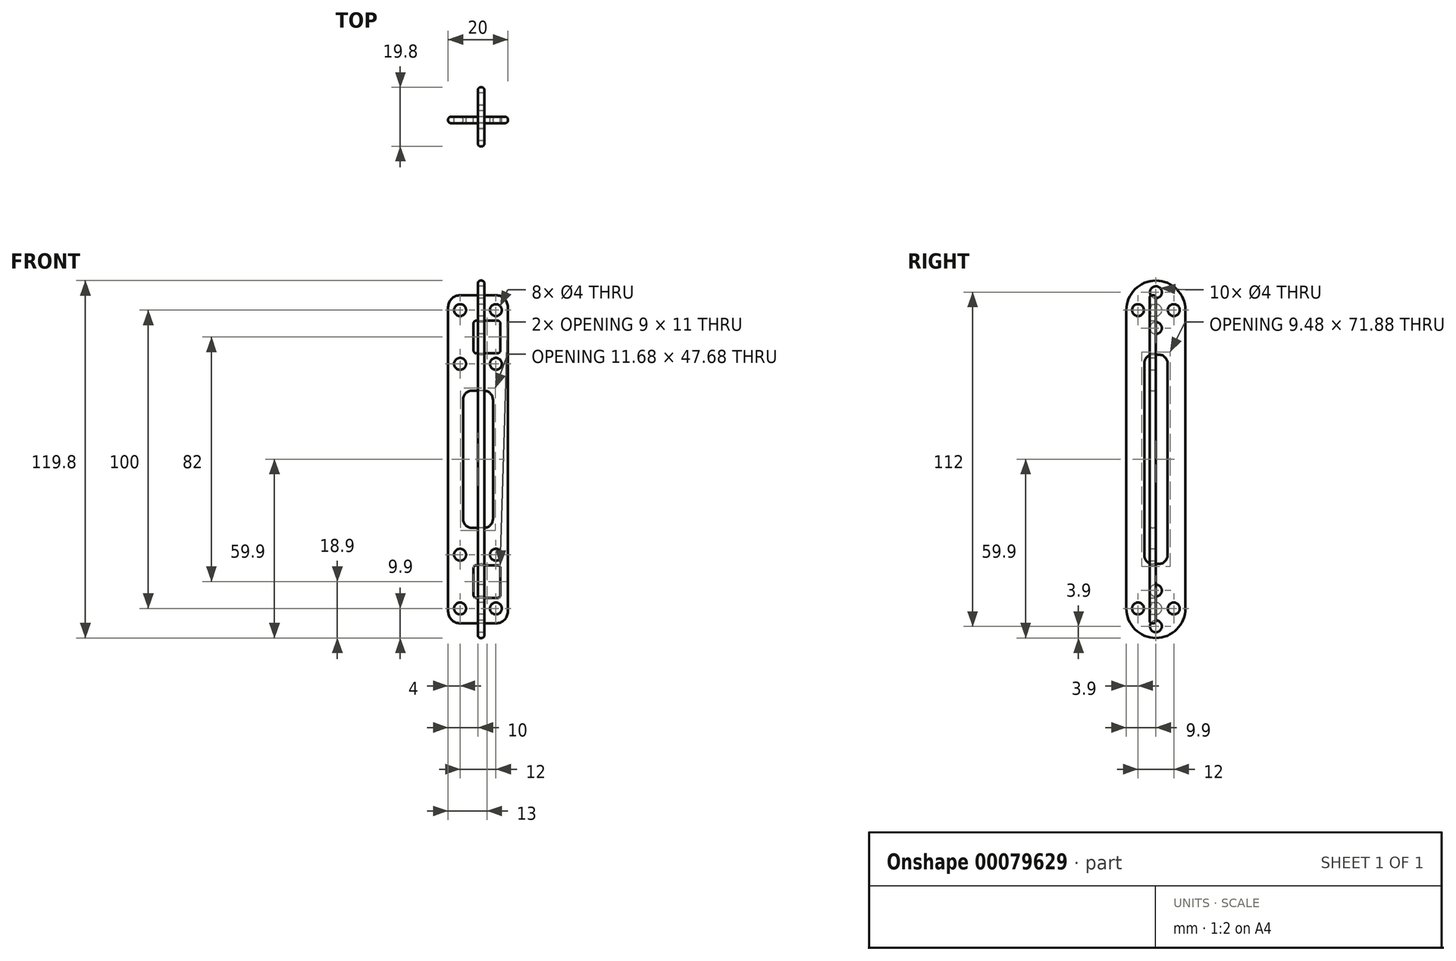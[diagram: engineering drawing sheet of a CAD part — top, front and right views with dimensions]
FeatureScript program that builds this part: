
annotation { "Feature Type Name" : "Feature", "Feature Type Description" : "" }
export const myFeature = defineFeature(function(context is Context, id is Id, definition is map)
    precondition{}
    {
        {
            assignVariable(context, id + "F0", {"name" : "tolerance", "anyValue" : 0.1});
        }
        {
            assignVariable(context, id + "F1", {"name" : "thickness", "anyValue" : 2.2 - getVariable(context, 'tolerance')});
        }
        {
            var Q0;
            Q0=qCreatedBy(makeId("Right.planeOp"),FACE);
            var sketch = newSketch(context, id + "F2", { "sketchPlane" : qUnion([Q0])});
            skLineSegment(sketch, "E0.rect.bottom", {"start": v(12, -9) * mm, "end": v(-12, -9) * mm});
            skLineSegment(sketch, "E0.rect.top", {"start": v(12, 27) * mm, "end": v(-12, 27) * mm});
            skLineSegment(sketch, "E0.rect.left", {"start": v(12, -9) * mm, "end": v(12, 27) * mm});
            skLineSegment(sketch, "E0.rect.right", {"start": v(-12, -9) * mm, "end": v(-12, 27) * mm});
            skPoint(sketch, "E0.rect.middle", {"position": v(0, 9) * mm});
            skCircle(sketch, "E1", {"center": v(0, 0) * mm, "radius": 8.9 * mm});
            skLineSegment(sketch, "E2", {"start": v(0, 27) * mm, "end": v(0, -9) * mm, "construction": true});
            skCircle(sketch, "E3", {"center": v(0, 0) * mm, "radius": 6 * mm, "construction": true});
            skCircle(sketch, "E4", {"center": v(0, -6) * mm, "radius": 2 * mm});
            skCircle(sketch, "E5.1.0", {"center": v(6, 0) * mm, "radius": 2 * mm});
            skCircle(sketch, "E5.2.0", {"center": v(0, 6) * mm, "radius": 2 * mm});
            skCircle(sketch, "E5.3.0", {"center": v(-6, 0) * mm, "radius": 2 * mm});
            skCircle(sketch, "E6", {"center": v(-4.24, 4.24) * mm, "radius": 0.8 * mm});
            skCircle(sketch, "E7.1.0", {"center": v(-4.24, -4.24) * mm, "radius": 0.8 * mm});
            skCircle(sketch, "E7.2.0", {"center": v(4.24, -4.24) * mm, "radius": 0.8 * mm});
            skCircle(sketch, "E7.3.0", {"center": v(4.24, 4.24) * mm, "radius": 0.8 * mm});
            skLineSegment(sketch, "E8", {"start": v(-6, 24) * mm, "end": v(6, 24) * mm, "construction": true});
            skCircle(sketch, "E9", {"center": v(-6, 24) * mm, "radius": 2 * mm});
            skCircle(sketch, "E10", {"center": v(0, 24) * mm, "radius": 2 * mm});
            skCircle(sketch, "E11", {"center": v(6, 24) * mm, "radius": 2 * mm});
            skPoint(sketch, "E12.center", {"position": v(0, 100) * mm});
            skLineSegment(sketch, "E13.rect.right", {"start": v(12, 109) * mm, "end": v(12, 73) * mm});
            skCircle(sketch, "E14", {"center": v(-6, 76) * mm, "radius": 2 * mm});
            skLineSegment(sketch, "E15", {"start": v(0, 73) * mm, "end": v(0, 109) * mm, "construction": true});
            skCircle(sketch, "E16", {"center": v(0, 100) * mm, "radius": 8.9 * mm});
            skLineSegment(sketch, "E13.rect.left", {"start": v(-12, 109) * mm, "end": v(-12, 73) * mm});
            skLineSegment(sketch, "E13.rect.bottom", {"start": v(-12, 109) * mm, "end": v(12, 109) * mm});
            skLineSegment(sketch, "E13.rect.top", {"start": v(-12, 73) * mm, "end": v(12, 73) * mm});
            skLineSegment(sketch, "E17", {"start": v(6, 76) * mm, "end": v(-6, 76) * mm, "construction": true});
            skCircle(sketch, "E18", {"center": v(0, 76) * mm, "radius": 2 * mm});
            skPoint(sketch, "E13.rect.middle", {"position": v(0, 91) * mm});
            skCircle(sketch, "E12.2.0", {"center": v(0, 94) * mm, "radius": 2 * mm});
            skCircle(sketch, "E12.1.0", {"center": v(-6, 100) * mm, "radius": 2 * mm});
            skCircle(sketch, "E19", {"center": v(0, 100) * mm, "radius": 6 * mm, "construction": true});
            skCircle(sketch, "E20", {"center": v(0, 106) * mm, "radius": 2 * mm});
            skCircle(sketch, "E21", {"center": v(-4.24, 104.24) * mm, "radius": 0.8 * mm});
            skCircle(sketch, "E12.3.0", {"center": v(6, 100) * mm, "radius": 2 * mm});
            skCircle(sketch, "E22.3.0", {"center": v(4.24, 104.24) * mm, "radius": 0.8 * mm});
            skCircle(sketch, "E22.2.0", {"center": v(4.24, 95.76) * mm, "radius": 0.8 * mm});
            skCircle(sketch, "E22.1.0", {"center": v(-4.24, 95.76) * mm, "radius": 0.8 * mm});
            skCircle(sketch, "E23", {"center": v(6, 76) * mm, "radius": 2 * mm});
            skSolve(sketch);
        }
        {
            var Q0;
            Q0=qCreatedBy(makeId("Front.planeOp"),FACE);
            var sketch = newSketch(context, id + "F3", { "sketchPlane" : qUnion([Q0])});
            skLineSegment(sketch, "E24", {"start": v(0, 22.5) * mm, "end": v(9, 22.5) * mm});
            skLineSegment(sketch, "E25", {"start": v(9, 22.5) * mm, "end": v(9, 27) * mm});
            skLineSegment(sketch, "E26", {"start": v(9, 27) * mm, "end": v(12, 27) * mm});
            skLineSegment(sketch, "E27", {"start": v(12, 27) * mm, "end": v(12, -9) * mm});
            skLineSegment(sketch, "E28", {"start": v(12, -9) * mm, "end": v(0, -9) * mm});
            skLineSegment(sketch, "E29", {"start": v(12, 8.9) * mm, "end": v(15, 8.9) * mm});
            skLineSegment(sketch, "E30", {"start": v(15, 8.9) * mm, "end": v(15, -8.9) * mm});
            skLineSegment(sketch, "E31", {"start": v(15, -8.9) * mm, "end": v(12, -8.9) * mm});
            skLineSegment(sketch, "E32", {"start": v(0, 1.45) * mm, "end": v(0, -56.88) * mm, "construction": true});
            skLineSegment(sketch, "E33", {"start": v(0, 0) * mm, "end": v(15, 0) * mm, "construction": true});
            skLineSegment(sketch, "E34.MirrorCS", {"start": v(-15, 8.9) * mm, "end": v(-15, -8.9) * mm});
            skLineSegment(sketch, "E35.MirrorCS", {"start": v(0, 22.5) * mm, "end": v(-9, 22.5) * mm});
            skLineSegment(sketch, "E36.MirrorCS", {"start": v(0, 0) * mm, "end": v(-15, 0) * mm, "construction": true});
            skLineSegment(sketch, "E37.MirrorCS", {"start": v(-9, 22.5) * mm, "end": v(-9, 27) * mm});
            skLineSegment(sketch, "E38.MirrorCS", {"start": v(-12, 8.9) * mm, "end": v(-15, 8.9) * mm});
            skLineSegment(sketch, "E39.MirrorCS", {"start": v(-12, -9) * mm, "end": v(0, -9) * mm});
            skLineSegment(sketch, "E40.MirrorCS", {"start": v(-12, 27) * mm, "end": v(-12, -9) * mm});
            skLineSegment(sketch, "E41.MirrorCS", {"start": v(-15, -8.9) * mm, "end": v(-12, -8.9) * mm});
            skLineSegment(sketch, "E42.MirrorCS", {"start": v(-9, 27) * mm, "end": v(-12, 27) * mm});
            skLineSegment(sketch, "E43.MirrorCS", {"start": v(0, 100) * mm, "end": v(-15, 100) * mm, "construction": true});
            skLineSegment(sketch, "E44.MirrorCS", {"start": v(0, 77.5) * mm, "end": v(-9, 77.5) * mm});
            skLineSegment(sketch, "E45", {"start": v(15, 108.9) * mm, "end": v(15, 91.1) * mm});
            skLineSegment(sketch, "E46.MirrorCS", {"start": v(-15, 108.9) * mm, "end": v(-15, 91.1) * mm});
            skLineSegment(sketch, "E47", {"start": v(0, 57.8) * mm, "end": v(0, 0) * mm, "construction": true});
            skLineSegment(sketch, "E48", {"start": v(12, 109) * mm, "end": v(0, 109) * mm});
            skLineSegment(sketch, "E49", {"start": v(12, 109) * mm, "end": v(12, 73) * mm});
            skLineSegment(sketch, "E50", {"start": v(0, 77.5) * mm, "end": v(9, 77.5) * mm});
            skLineSegment(sketch, "E51.MirrorCS", {"start": v(-12, 109) * mm, "end": v(0, 109) * mm});
            skLineSegment(sketch, "E52.MirrorCS", {"start": v(-12, 109) * mm, "end": v(-12, 73) * mm});
            skLineSegment(sketch, "E53", {"start": v(0, 100) * mm, "end": v(15, 100) * mm, "construction": true});
            skLineSegment(sketch, "E54", {"start": v(12, 108.9) * mm, "end": v(15, 108.9) * mm});
            skLineSegment(sketch, "E55", {"start": v(9, 73) * mm, "end": v(12, 73) * mm});
            skLineSegment(sketch, "E56", {"start": v(9, 73) * mm, "end": v(9, 77.5) * mm});
            skLineSegment(sketch, "E57.MirrorCS", {"start": v(-9, 73) * mm, "end": v(-12, 73) * mm});
            skLineSegment(sketch, "E58.MirrorCS", {"start": v(-12, 108.9) * mm, "end": v(-15, 108.9) * mm});
            skLineSegment(sketch, "E59.MirrorCS", {"start": v(-9, 73) * mm, "end": v(-9, 77.5) * mm});
            skLineSegment(sketch, "E60.MirrorCS", {"start": v(-15, 91.1) * mm, "end": v(-12, 91.1) * mm});
            skLineSegment(sketch, "E61", {"start": v(15, 91.1) * mm, "end": v(12, 91.1) * mm});
            skLineSegment(sketch, "E62.bottom", {"start": v(-6, 18) * mm, "end": v(6, 18) * mm, "construction": true});
            skLineSegment(sketch, "E62.top", {"start": v(-6, 0) * mm, "end": v(6, 0) * mm, "construction": true});
            skLineSegment(sketch, "E62.left", {"start": v(-6, 18) * mm, "end": v(-6, 0) * mm, "construction": true});
            skLineSegment(sketch, "E62.right", {"start": v(6, 18) * mm, "end": v(6, 0) * mm, "construction": true});
            skCircle(sketch, "E63", {"center": v(6, 0) * mm, "radius": 2 * mm});
            skCircle(sketch, "E64", {"center": v(-6, 0) * mm, "radius": 2 * mm});
            skCircle(sketch, "E65", {"center": v(-6, 18) * mm, "radius": 2 * mm});
            skCircle(sketch, "E66", {"center": v(6, 18) * mm, "radius": 2 * mm});
            skLineSegment(sketch, "E67.left", {"start": v(-6, 100) * mm, "end": v(-6, 82) * mm, "construction": true});
            skCircle(sketch, "E68", {"center": v(-6, 100) * mm, "radius": 2 * mm});
            skLineSegment(sketch, "E67.right", {"start": v(6, 100) * mm, "end": v(6, 82) * mm, "construction": true});
            skLineSegment(sketch, "E67.bottom", {"start": v(-6, 100) * mm, "end": v(6, 100) * mm, "construction": true});
            skCircle(sketch, "E69", {"center": v(6, 100) * mm, "radius": 2 * mm});
            skCircle(sketch, "E70", {"center": v(6, 82) * mm, "radius": 2 * mm});
            skLineSegment(sketch, "E67.top", {"start": v(-6, 82) * mm, "end": v(6, 82) * mm, "construction": true});
            skCircle(sketch, "E71", {"center": v(-6, 82) * mm, "radius": 2 * mm});
            skLineSegment(sketch, "E72.rect.bottom", {"start": v(7.5, 96.5) * mm, "end": v(-7.5, 96.5) * mm});
            skLineSegment(sketch, "E72.rect.top", {"start": v(7.5, 85.5) * mm, "end": v(-7.5, 85.5) * mm});
            skLineSegment(sketch, "E72.rect.left", {"start": v(7.5, 96.5) * mm, "end": v(7.5, 85.5) * mm});
            skLineSegment(sketch, "E72.rect.right", {"start": v(-7.5, 96.5) * mm, "end": v(-7.5, 85.5) * mm});
            skPoint(sketch, "E72.rect.middle", {"position": v(0, 91) * mm});
            skLineSegment(sketch, "E73.rect.bottom", {"start": v(7.5, 3.5) * mm, "end": v(-7.5, 3.5) * mm});
            skLineSegment(sketch, "E73.rect.top", {"start": v(7.5, 14.5) * mm, "end": v(-7.5, 14.5) * mm});
            skLineSegment(sketch, "E73.rect.left", {"start": v(7.5, 3.5) * mm, "end": v(7.5, 14.5) * mm});
            skLineSegment(sketch, "E73.rect.right", {"start": v(-7.5, 3.5) * mm, "end": v(-7.5, 14.5) * mm});
            skPoint(sketch, "E73.rect.middle", {"position": v(0, 9) * mm});
            skSolve(sketch);
        }
        {
            var Q0;
            Q0=qCreatedBy(makeId("Front.planeOp"),FACE);
            var sketch = newSketch(context, id + "F4", { "sketchPlane" : qUnion([Q0])});
            skLineSegment(sketch, "E74.rect.bottom", {"start": v(6, 105) * mm, "end": v(-6, 105) * mm});
            skLineSegment(sketch, "E74.rect.top", {"start": v(6, -5) * mm, "end": v(-6, -5) * mm});
            skLineSegment(sketch, "E74.rect.left", {"start": v(10, 101) * mm, "end": v(10, -1) * mm});
            skLineSegment(sketch, "E74.rect.right", {"start": v(-10, 101) * mm, "end": v(-10, -1) * mm});
            skPoint(sketch, "E74.rect.middle", {"position": v(0, 50) * mm});
            skCircle(sketch, "E75", {"center": v(-6, 18) * mm, "radius": 2 * mm});
            skCircle(sketch, "E76", {"center": v(6, 18) * mm, "radius": 2 * mm});
            skCircle(sketch, "E77", {"center": v(-6, 0) * mm, "radius": 2 * mm});
            skCircle(sketch, "E78", {"center": v(6, 0) * mm, "radius": 2 * mm});
            skCircle(sketch, "E79", {"center": v(-6, 82) * mm, "radius": 2 * mm});
            skCircle(sketch, "E80", {"center": v(6, 82) * mm, "radius": 2 * mm});
            skCircle(sketch, "E81", {"center": v(-6, 100) * mm, "radius": 2 * mm});
            skCircle(sketch, "E82", {"center": v(6, 100) * mm, "radius": 2 * mm});
            skPoint(sketch, "E83.visualSharp", {"position": v(-10, 105) * mm});
            skArc(sketch, "E83.filletArc", {"start": v(-6, 105) * mm, "mid": v(-8.83, 103.83) * mm, "end": v(-10, 101) * mm});
            skPoint(sketch, "E84.visualSharp", {"position": v(10, 105) * mm});
            skArc(sketch, "E84.filletArc", {"start": v(10, 101) * mm, "mid": v(8.83, 103.83) * mm, "end": v(6, 105) * mm});
            skPoint(sketch, "E85.visualSharp", {"position": v(10, -5) * mm});
            skArc(sketch, "E85.filletArc", {"start": v(6, -5) * mm, "mid": v(8.83, -3.83) * mm, "end": v(10, -1) * mm});
            skPoint(sketch, "E86.visualSharp", {"position": v(-10, -5) * mm});
            skArc(sketch, "E86.filletArc", {"start": v(-10, -1) * mm, "mid": v(-8.83, -3.83) * mm, "end": v(-6, -5) * mm});
            skLineSegment(sketch, "E87.rect.bottom", {"start": v(2, 27) * mm, "end": v(-2, 27) * mm});
            skLineSegment(sketch, "E87.rect.top", {"start": v(2, 73) * mm, "end": v(-2, 73) * mm});
            skLineSegment(sketch, "E87.rect.left", {"start": v(5, 30) * mm, "end": v(5, 70) * mm});
            skLineSegment(sketch, "E87.rect.right", {"start": v(-5, 30) * mm, "end": v(-5, 70) * mm});
            skPoint(sketch, "E88.visualSharp", {"position": v(-5, 73) * mm});
            skArc(sketch, "E88.filletArc", {"start": v(-2, 73) * mm, "mid": v(-4.12, 72.12) * mm, "end": v(-5, 70) * mm});
            skPoint(sketch, "E89.visualSharp", {"position": v(5, 73) * mm});
            skArc(sketch, "E89.filletArc", {"start": v(5, 70) * mm, "mid": v(4.12, 72.12) * mm, "end": v(2, 73) * mm});
            skPoint(sketch, "E90.visualSharp", {"position": v(5, 27) * mm});
            skArc(sketch, "E90.filletArc", {"start": v(2, 27) * mm, "mid": v(4.12, 27.88) * mm, "end": v(5, 30) * mm});
            skPoint(sketch, "E91.visualSharp", {"position": v(-5, 27) * mm});
            skArc(sketch, "E91.filletArc", {"start": v(-5, 30) * mm, "mid": v(-4.12, 27.88) * mm, "end": v(-2, 27) * mm});
            skSolve(sketch);
        }
        {
            var Q0;
            Q0=makeQuery(id+"F4.imprint","IMPRINT",FACE,{"disambiguationData":[TD([[makeQuery(id+"F4.imprint","IMPRINT",EDGE,{"derivedFrom":sQuery(id+"F4.wireOp",EDGE,"E74.rect.bottom")}),1.0]])]});
            extrude(context, id + "F5", {"entities" : qUnion([Q0]), "depth" : (getVariable(context, 'thickness')) * mm});
        }
        {
            var Q0;
            Q0=qCreatedBy(makeId("Front.planeOp"),FACE);
            var sketch = newSketch(context, id + "F6", { "sketchPlane" : qUnion([Q0])});
            skLineSegment(sketch, "E92.rect.bottom", {"start": v(-0.5, 14.5) * mm, "end": v(6.5, 14.5) * mm});
            skLineSegment(sketch, "E92.rect.top", {"start": v(-0.5, 3.5) * mm, "end": v(6.5, 3.5) * mm});
            skLineSegment(sketch, "E92.rect.left", {"start": v(-1.5, 13.5) * mm, "end": v(-1.5, 4.5) * mm});
            skLineSegment(sketch, "E92.rect.right", {"start": v(7.5, 13.5) * mm, "end": v(7.5, 4.5) * mm});
            skPoint(sketch, "E92.rect.middle", {"position": v(3, 9) * mm});
            skPoint(sketch, "E93.visualSharp", {"position": v(-1.5, 14.5) * mm});
            skArc(sketch, "E93.filletArc", {"start": v(-0.5, 14.5) * mm, "mid": v(-1.2, 14.2) * mm, "end": v(-1.5, 13.5) * mm});
            skPoint(sketch, "E94.visualSharp", {"position": v(7.5, 14.5) * mm});
            skArc(sketch, "E94.filletArc", {"start": v(7.5, 13.5) * mm, "mid": v(7.2, 14.2) * mm, "end": v(6.5, 14.5) * mm});
            skPoint(sketch, "E95.visualSharp", {"position": v(7.5, 3.5) * mm});
            skArc(sketch, "E95.filletArc", {"start": v(6.5, 3.5) * mm, "mid": v(7.2, 3.8) * mm, "end": v(7.5, 4.5) * mm});
            skPoint(sketch, "E96.visualSharp", {"position": v(-1.5, 3.5) * mm});
            skArc(sketch, "E96.filletArc", {"start": v(-1.5, 4.5) * mm, "mid": v(-1.2, 3.8) * mm, "end": v(-0.5, 3.5) * mm});
            skPoint(sketch, "E97.visualSharp", {"position": v(7.5, 96.5) * mm});
            skPoint(sketch, "E98.visualSharp", {"position": v(-1.5, 85.5) * mm});
            skPoint(sketch, "E99.rect.middle", {"position": v(3, 91) * mm});
            skPoint(sketch, "E100.visualSharp", {"position": v(7.5, 85.5) * mm});
            skLineSegment(sketch, "E99.rect.top", {"start": v(-0.5, 85.5) * mm, "end": v(6.5, 85.5) * mm});
            skLineSegment(sketch, "E99.rect.right", {"start": v(7.5, 95.5) * mm, "end": v(7.5, 86.5) * mm});
            skPoint(sketch, "E101.visualSharp", {"position": v(-1.5, 96.5) * mm});
            skLineSegment(sketch, "E99.rect.bottom", {"start": v(-0.5, 96.5) * mm, "end": v(6.5, 96.5) * mm});
            skLineSegment(sketch, "E99.rect.left", {"start": v(-1.5, 95.5) * mm, "end": v(-1.5, 86.5) * mm});
            skArc(sketch, "E98.filletArc", {"start": v(-1.5, 86.5) * mm, "mid": v(-1.2, 85.8) * mm, "end": v(-0.5, 85.5) * mm});
            skArc(sketch, "E101.filletArc", {"start": v(-0.5, 96.5) * mm, "mid": v(-1.2, 96.2) * mm, "end": v(-1.5, 95.5) * mm});
            skArc(sketch, "E97.filletArc", {"start": v(7.5, 95.5) * mm, "mid": v(7.2, 96.2) * mm, "end": v(6.5, 96.5) * mm});
            skArc(sketch, "E100.filletArc", {"start": v(6.5, 85.5) * mm, "mid": v(7.2, 85.8) * mm, "end": v(7.5, 86.5) * mm});
            skSolve(sketch);
        }
        {
            var Q0;
            Q0=qSketchRegion(id+"F6",true);
            extrude(context, id + "F7", {"entities" : qUnion([Q0]), "operationType" : NewBodyOperationType.REMOVE, "endBound" : BoundingType.UP_TO_NEXT, "depth" : 25 * mm});
        }
        {
            var Q0;
            Q0=makeQuery(id+"F5.opExtrude","SWEPT_FACE",FACE,{"disambiguationData":[OSD([sQuery(id+"F4.wireOp",EDGE,"E74.rect.left")])]});
            var Q1;
            Q1=makeQuery(id+"F5.opExtrude","SWEPT_FACE",FACE,{"disambiguationData":[OSD([sQuery(id+"F4.wireOp",EDGE,"E87.rect.right")])]});
            fillet(context, id + "F8", {"entities" : qUnion([Q0, Q1]), "radius" : (getVariable(context, 'thickness') / 2.5) * mm, "tangentPropagation" : true, "allowEdgeOverflow" : false});
        }
        {
            var Q0;
            Q0=qCreatedBy(makeId("Right.planeOp"),FACE);
            var sketch = newSketch(context, id + "F9", { "sketchPlane" : qUnion([Q0])});
            skCircle(sketch, "E102", {"center": v(0, 100) * mm, "radius": 9.9 * mm});
            skCircle(sketch, "E103", {"center": v(0, 0) * mm, "radius": 9.9 * mm});
            skLineSegment(sketch, "E104", {"start": v(9.9, 0) * mm, "end": v(9.9, 100) * mm});
            skLineSegment(sketch, "E105", {"start": v(-9.9, 100) * mm, "end": v(-9.9, 0) * mm});
            skCircle(sketch, "E106", {"center": v(0, 106) * mm, "radius": 2 * mm});
            skCircle(sketch, "E107", {"center": v(-6, 100) * mm, "radius": 2 * mm});
            skCircle(sketch, "E108", {"center": v(6, 100) * mm, "radius": 2 * mm});
            skCircle(sketch, "E109", {"center": v(0, 94) * mm, "radius": 2 * mm});
            skCircle(sketch, "E110", {"center": v(-6, 0) * mm, "radius": 2 * mm});
            skCircle(sketch, "E111", {"center": v(0, 6) * mm, "radius": 2 * mm});
            skCircle(sketch, "E112", {"center": v(6, 0) * mm, "radius": 2 * mm});
            skCircle(sketch, "E113", {"center": v(0, -6) * mm, "radius": 2 * mm});
            skCircle(sketch, "E114", {"center": v(0, 100) * mm, "radius": 2 * mm});
            skCircle(sketch, "E115", {"center": v(0, 0) * mm, "radius": 2 * mm});
            skLineSegment(sketch, "E116.rect.bottom", {"start": v(0.9, 14.9) * mm, "end": v(-0.9, 14.9) * mm});
            skLineSegment(sketch, "E116.rect.top", {"start": v(0.9, 85.1) * mm, "end": v(-0.9, 85.1) * mm});
            skLineSegment(sketch, "E116.rect.left", {"start": v(3.9, 17.9) * mm, "end": v(3.9, 82.1) * mm});
            skLineSegment(sketch, "E116.rect.right", {"start": v(-3.9, 17.9) * mm, "end": v(-3.9, 82.1) * mm});
            skPoint(sketch, "E116.rect.middle", {"position": v(0, 50) * mm});
            skLineSegment(sketch, "E117", {"start": v(0, 100) * mm, "end": v(0, 0) * mm, "construction": true});
            skPoint(sketch, "E118.visualSharp", {"position": v(-3.9, 14.9) * mm});
            skArc(sketch, "E118.filletArc", {"start": v(-3.9, 17.9) * mm, "mid": v(-3.02, 15.78) * mm, "end": v(-0.9, 14.9) * mm});
            skPoint(sketch, "E119.visualSharp", {"position": v(3.9, 14.9) * mm});
            skArc(sketch, "E119.filletArc", {"start": v(0.9, 14.9) * mm, "mid": v(3.02, 15.78) * mm, "end": v(3.9, 17.9) * mm});
            skPoint(sketch, "E120.visualSharp", {"position": v(-3.9, 85.1) * mm});
            skArc(sketch, "E120.filletArc", {"start": v(-0.9, 85.1) * mm, "mid": v(-3.02, 84.22) * mm, "end": v(-3.9, 82.1) * mm});
            skPoint(sketch, "E121.visualSharp", {"position": v(3.9, 85.1) * mm});
            skArc(sketch, "E121.filletArc", {"start": v(3.9, 82.1) * mm, "mid": v(3.02, 84.22) * mm, "end": v(0.9, 85.1) * mm});
            skSolve(sketch);
        }
        {
            var Q0;
            Q0=qSketchRegion(id+"F9",true);
            extrude(context, id + "F10", {"entities" : qUnion([Q0]), "depth" : (getVariable(context, 'thickness')) * mm});
        }
        {
            var Q0;
            Q0=makeQuery(id+"F10.opExtrude","SWEPT_FACE",FACE,{"disambiguationData":[OSD([sQuery(id+"F9.wireOp",EDGE,"E104")])]});
            var Q1;
            Q1=makeQuery(id+"F10.opExtrude","SWEPT_FACE",FACE,{"disambiguationData":[OSD([sQuery(id+"F9.wireOp",EDGE,"E116.rect.right")])]});
            fillet(context, id + "F11", {"entities" : qUnion([Q0, Q1]), "radius" : (getVariable(context, 'thickness') / 2.5) * mm, "tangentPropagation" : true, "allowEdgeOverflow" : false});
        }
    });
